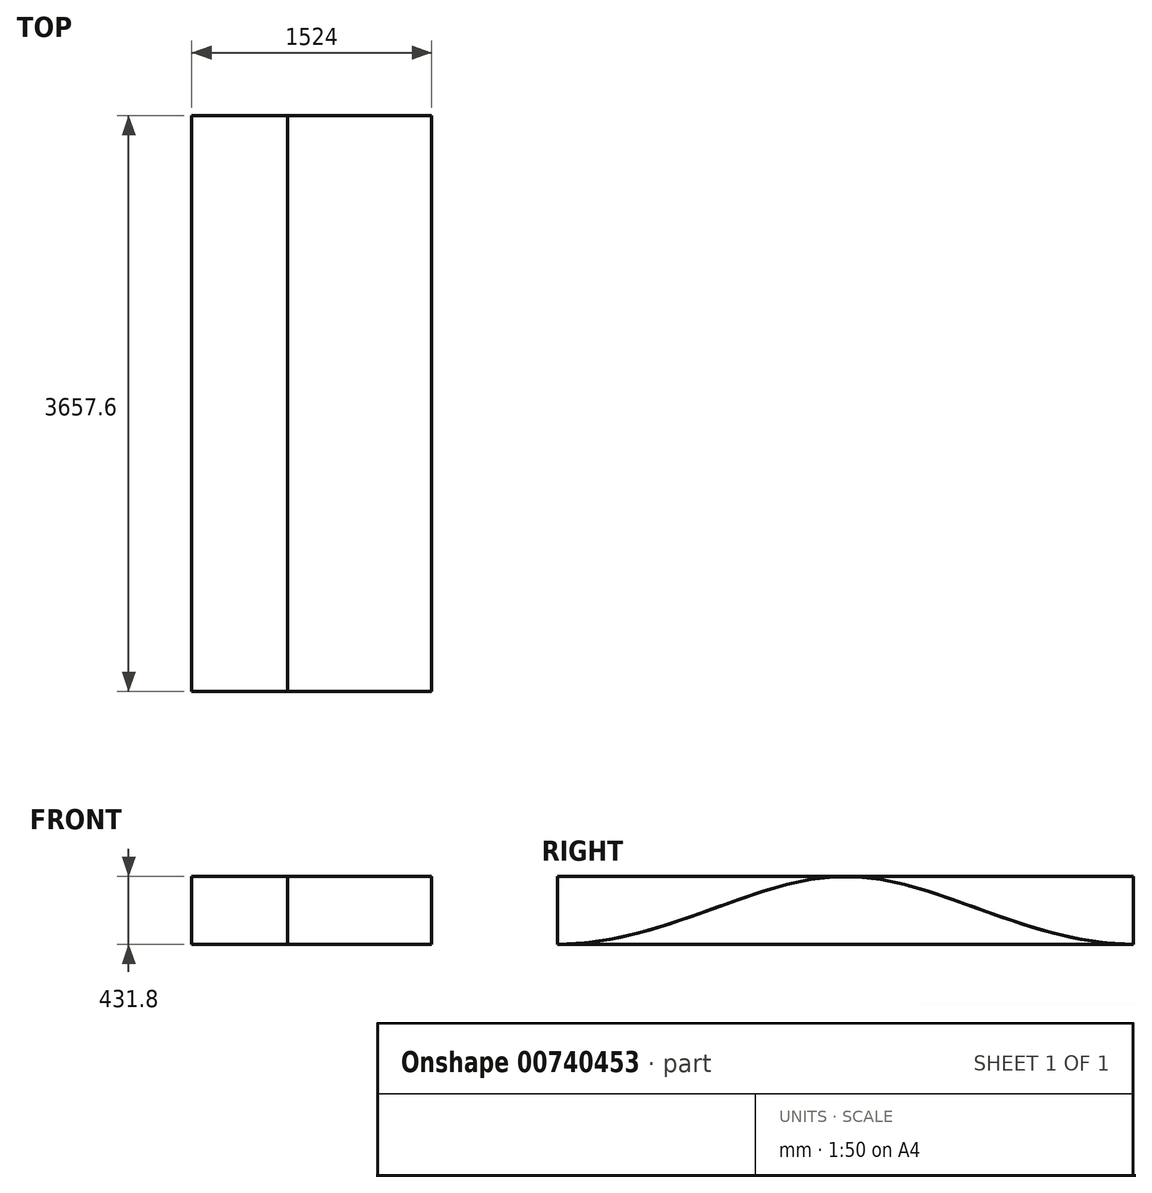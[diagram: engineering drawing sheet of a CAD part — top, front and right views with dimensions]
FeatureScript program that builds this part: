
annotation { "Feature Type Name" : "Feature", "Feature Type Description" : "" }
export const myFeature = defineFeature(function(context is Context, id is Id, definition is map)
    precondition{}
    {
        {
            var Q0;
            Q0=qCreatedBy(makeId("Top.planeOp"),FACE);
            var sketch = newSketch(context, id + "F0", { "sketchPlane" : qUnion([Q0])});
            skLineSegment(sketch, "E0.bottom", {"start": v(304.8, -1828.8) * mm, "end": v(-304.8, -1828.8) * mm});
            skLineSegment(sketch, "E0.top", {"start": v(304.8, 1828.8) * mm, "end": v(-304.8, 1828.8) * mm});
            skLineSegment(sketch, "E0.left", {"start": v(304.8, -1828.8) * mm, "end": v(304.8, 1828.8) * mm});
            skLineSegment(sketch, "E0.right", {"start": v(-304.8, -1828.8) * mm, "end": v(-304.8, 1828.8) * mm});
            skPoint(sketch, "E0.middle", {"position": v(0, 0) * mm});
            skSolve(sketch);
        }
        {
            var Q0;
            Q0=makeQuery(id+"F0.imprint","IMPRINT",FACE,{"disambiguationData":[TD([[makeQuery(id+"F0.imprint","IMPRINT",EDGE,{"derivedFrom":sQuery(id+"F0.wireOp",EDGE,"E0.bottom")}),-1.0]])]});
            extrude(context, id + "F1", {"entities" : qUnion([Q0]), "depth" : 431.8 * mm, "offsetDistance" : 25 * mm});
        }
        {
            var Q0;
            Q0=makeQuery(id+"F1.opExtrude","SWEPT_FACE",FACE,{"disambiguationData":[OSD([sQuery(id+"F0.wireOp",EDGE,"E0.left")])]});
            var sketch = newSketch(context, id + "F2", { "sketchPlane" : qUnion([Q0])});
            skFitSpline(sketch, "E1", {"points": [v(-1828.8, 0) * mm, v(0, 431.8) * mm, v(1828.8, 0) * mm], "startDerivative": vector(4108.55, 0) * mm, "endDerivative": vector(4108.55, 0) * mm});
            skLineSegment(sketch, "E2", {"start": v(0, -265.95) * mm, "end": v(0, 588.02) * mm, "construction": true});
            skLineSegment(sketch, "E3", {"start": v(-1828.8, 0) * mm, "end": v(1828.8, 0) * mm});
            skSolve(sketch);
        }
        {
            var Q0;
            {var subQ0=sQuery(id+"F2.wireOp",EDGE,"E3");Q0=makeQuery(id+"F2.imprint","IMPRINT",FACE,{"disambiguationData":[TD([[makeQuery(id+"F2.imprint","IMPRINT",EDGE,{"derivedFrom":subQ0}),1.0]])]});}
            extrude(context, id + "F3", {"entities" : qUnion([Q0]), "operationType" : NewBodyOperationType.ADD, "depth" : 914.4 * mm, "offsetDistance" : 25 * mm});
        }
    });
